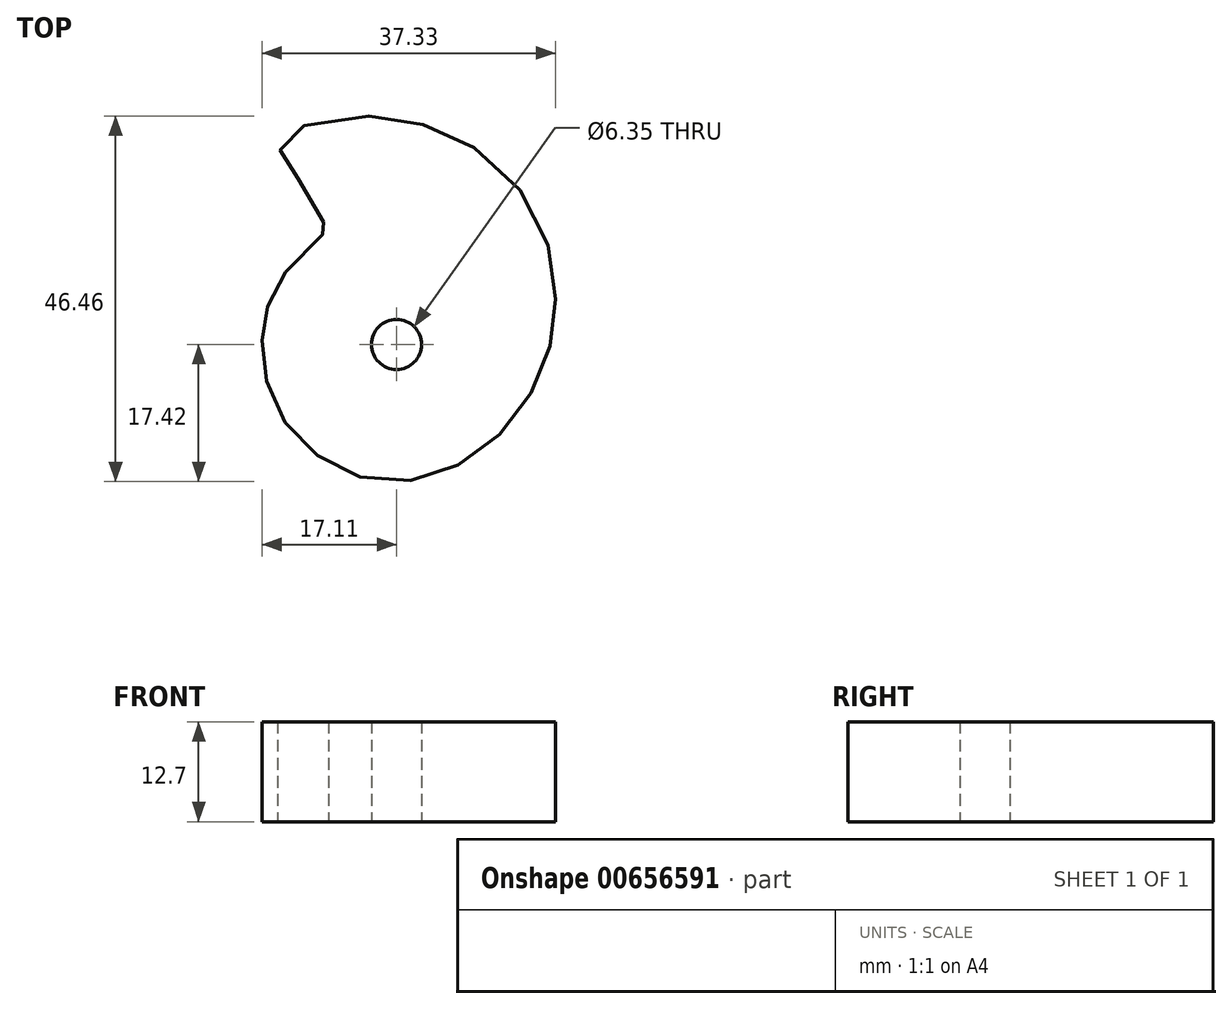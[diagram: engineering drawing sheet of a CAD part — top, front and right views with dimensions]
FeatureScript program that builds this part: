
annotation { "Feature Type Name" : "Feature", "Feature Type Description" : "" }
export const myFeature = defineFeature(function(context is Context, id is Id, definition is map)
    precondition{}
    {
        {
            var Q0;
            Q0=qCreatedBy(makeId("Top.planeOp"),FACE);
            var sketch = newSketch(context, id + "F0", { "sketchPlane" : qUnion([Q0])});
            skCircle(sketch, "E0", {"center": v(0, 0) * mm, "radius": 3.17 * mm});
            skFitSpline(sketch, "E1", {"points": [v(-16.35, 4.8) * mm, v(-17.03, 1.7) * mm, v(-16.92, -2.38) * mm, v(-15.39, -7.8) * mm, v(-11.88, -12.5) * mm, v(-6.85, -16.06) * mm, v(0, -17.41) * mm, v(6.83, -15.77) * mm, v(12.84, -11.64) * mm, v(17.4, -5.54) * mm, v(19.78, 1.02) * mm, v(20.13, 7.5) * mm, v(17.65, 16.58) * mm, v(10.33, 24.72) * mm, v(2.3, 28.23) * mm, v(-6.88, 28.84) * mm, v(-15.02, 25.86) * mm, v(-14, 23.68) * mm, v(-12.33, 20.7) * mm, v(-9, 15.1) * mm, v(-8.72, 14.64) * mm, v(-8.63, 14.51) * mm, v(-9.5, 13.9) * mm, v(-14.88, 8.13) * mm, v(-16.35, 4.8) * mm]});
            skSolve(sketch);
        }
        {
            var Q0;
            Q0 = qSketchRegion(id + "F0", true);
            extrude(context, id + "F1", {"entities" : qUnion([Q0]), "depth" : 12.7 * mm, "offsetDistance" : 25.4 * mm});
        }
    });
